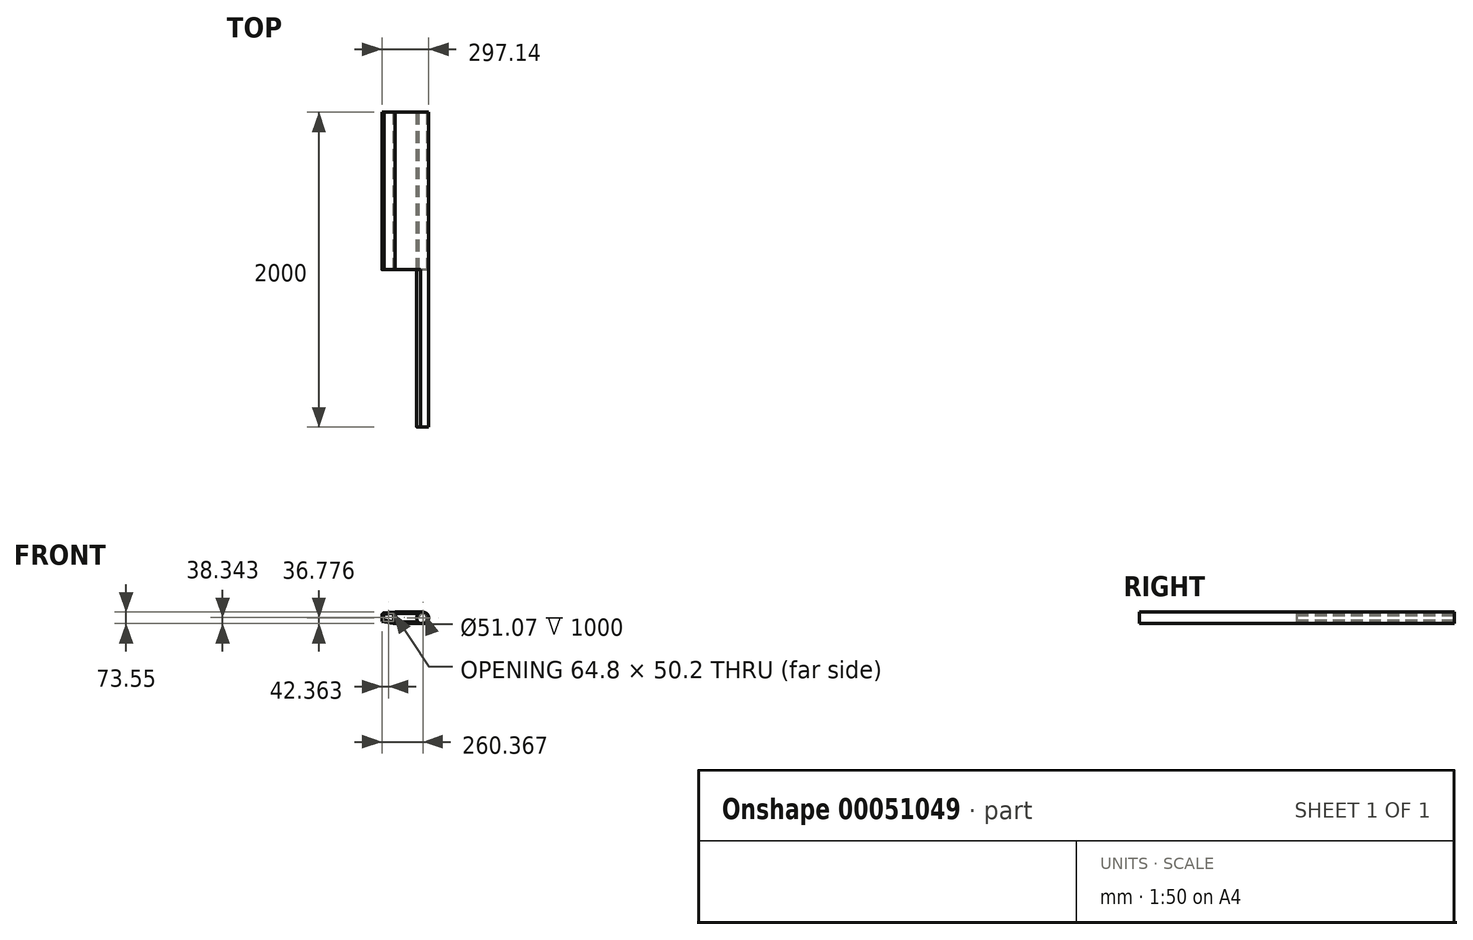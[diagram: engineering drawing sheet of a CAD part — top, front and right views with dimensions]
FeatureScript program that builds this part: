
annotation { "Feature Type Name" : "Feature", "Feature Type Description" : "" }
export const myFeature = defineFeature(function(context is Context, id is Id, definition is map)
    precondition{}
    {
        {
            var Q0;
            Q0=qCreatedBy(makeId("Front.planeOp"),FACE);
            var sketch = newSketch(context, id + "F0", { "sketchPlane" : qUnion([Q0])});
            skLineSegment(sketch, "E0", {"start": v(-73.23, 42.97) * mm, "end": v(104.82, 42.97) * mm});
            skArc(sketch, "E1", {"start": v(104.82, -30.58) * mm, "mid": v(141.6, 6.2) * mm, "end": v(104.82, 42.97) * mm});
            skLineSegment(sketch, "E2", {"start": v(104.82, -30.58) * mm, "end": v(-80.24, -30.58) * mm});
            skLineSegment(sketch, "E3", {"start": v(-80.24, -30.58) * mm, "end": v(-155.55, -17.15) * mm});
            skLineSegment(sketch, "E4", {"start": v(-155.55, -17.15) * mm, "end": v(-155.55, 23.13) * mm});
            skArc(sketch, "E5", {"start": v(-142.12, 38.3) * mm, "mid": v(-151.7, 33.26) * mm, "end": v(-155.55, 23.13) * mm});
            skLineSegment(sketch, "E6", {"start": v(-73.23, 42.97) * mm, "end": v(-142.12, 38.3) * mm});
            skLineSegment(sketch, "E7", {"start": v(-145.59, 23.13) * mm, "end": v(-145.59, -5.96) * mm});
            skLineSegment(sketch, "E8", {"start": v(-145.59, -5.96) * mm, "end": v(-80.79, -17.34) * mm});
            skLineSegment(sketch, "E9", {"start": v(-80.79, -17.34) * mm, "end": v(-80.79, 32.86) * mm});
            skLineSegment(sketch, "E10", {"start": v(-80.79, 32.86) * mm, "end": v(-138.58, 29.07) * mm});
            skArc(sketch, "E11", {"start": v(-138.58, 29.07) * mm, "mid": v(-143.07, 27.26) * mm, "end": v(-145.59, 23.13) * mm});
            skCircle(sketch, "E12", {"center": v(104.82, 6.2) * mm, "radius": 25.53 * mm});
            skArc(sketch, "E13", {"start": v(75.56, 32.97) * mm, "mid": v(65.19, 7.84) * mm, "end": v(73.44, -18.06) * mm});
            skLineSegment(sketch, "E14", {"start": v(75.56, 32.97) * mm, "end": v(-69.74, 32.97) * mm});
            skLineSegment(sketch, "E15", {"start": v(-69.74, 32.97) * mm, "end": v(-69.74, -18.06) * mm});
            skLineSegment(sketch, "E16", {"start": v(-69.74, -18.06) * mm, "end": v(73.44, -18.06) * mm});
            skSolve(sketch);
        }
        {
            var Q0;
            Q0=makeQuery(id+"F0.imprint","IMPRINT",FACE,{"disambiguationData":[TD([[makeQuery(id+"F0.imprint","IMPRINT",EDGE,{"derivedFrom":sQuery(id+"F0.wireOp",EDGE,"E0")}),-1.0]])]});
            extrude(context, id + "F1", {"entities" : qUnion([Q0]), "depth" : 1000 * mm});
        }
        {
            var Q0;
            Q0=makeQuery(id+"F1.opExtrude","CAP_FACE",FACE,{"disambiguationData":[OSD([sQuery(id+"F0.wireOp",EDGE,"E0"),sQuery(id+"F0.wireOp",EDGE,"E1"),sQuery(id+"F0.wireOp",EDGE,"E2"),sQuery(id+"F0.wireOp",EDGE,"E3"),sQuery(id+"F0.wireOp",EDGE,"E4"),sQuery(id+"F0.wireOp",EDGE,"E5"),sQuery(id+"F0.wireOp",EDGE,"E6"),sQuery(id+"F0.wireOp",EDGE,"E7"),sQuery(id+"F0.wireOp",EDGE,"E8"),sQuery(id+"F0.wireOp",EDGE,"E9"),sQuery(id+"F0.wireOp",EDGE,"E10"),sQuery(id+"F0.wireOp",EDGE,"E11"),sQuery(id+"F0.wireOp",EDGE,"E12"),sQuery(id+"F0.wireOp",EDGE,"E13"),sQuery(id+"F0.wireOp",EDGE,"E14"),sQuery(id+"F0.wireOp",EDGE,"E15"),sQuery(id+"F0.wireOp",EDGE,"E16")])],"isStart":false});
            var sketch = newSketch(context, id + "F2", { "sketchPlane" : qUnion([Q0])});
            skArc(sketch, "E17.0", {"start": v(104.82, -30.58) * mm, "mid": v(141.6, 6.2) * mm, "end": v(104.82, 42.97) * mm});
            skArc(sketch, "E18.0", {"start": v(75.56, 32.97) * mm, "mid": v(65.19, 7.84) * mm, "end": v(73.44, -18.06) * mm});
            skCircle(sketch, "E19", {"center": v(104.82, 6.2) * mm, "radius": 39.66 * mm});
            skSolve(sketch);
        }
        {
            var Q0;
            {var subQ4=sQuery(id+"F2.wireOp",EDGE,"E17.0");Q0=makeQuery(id+"F2.imprint","IMPRINT",FACE,{"disambiguationData":[TD([[makeQuery(id+"F2.imprint","IMPRINT",EDGE,{"derivedFrom":subQ4}),1.0]])]});}
            var Q1;
            Q1=makeQuery(id+"F2.imprint","IMPRINT",FACE,{"disambiguationData":[TD([[makeQuery(id+"F2.imprint","IMPRINT",EDGE,{"derivedFrom":makeQuery(id+"F1.opExtrude","CAP_EDGE",EDGE,{"disambiguationData":[OSD([sQuery(id+"F0.wireOp",EDGE,"E12")])],"isStart":false})}),1.0]])]});
            extrude(context, id + "F3", {"entities" : qUnion([Q0, Q1]), "operationType" : NewBodyOperationType.ADD, "depth" : 1000 * mm});
        }
    });
